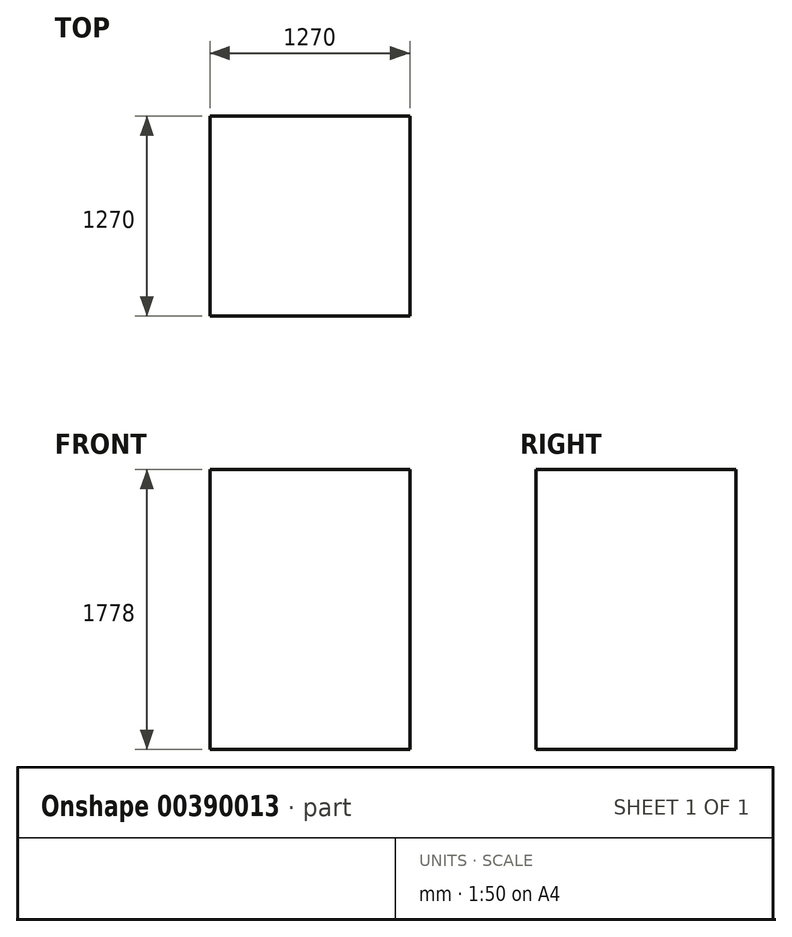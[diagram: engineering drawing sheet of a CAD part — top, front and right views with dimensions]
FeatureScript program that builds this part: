
annotation { "Feature Type Name" : "Feature", "Feature Type Description" : "" }
export const myFeature = defineFeature(function(context is Context, id is Id, definition is map)
    precondition{}
    {
        {
            var Q0;
            Q0=qCreatedBy(makeId("Top.planeOp"),FACE);
            var sketch = newSketch(context, id + "F0", { "sketchPlane" : qUnion([Q0])});
            skLineSegment(sketch, "E0.bottom", {"start": v(635, 635) * mm, "end": v(-635, 635) * mm});
            skLineSegment(sketch, "E0.top", {"start": v(635, -635) * mm, "end": v(-635, -635) * mm});
            skLineSegment(sketch, "E0.left", {"start": v(635, 635) * mm, "end": v(635, -635) * mm});
            skLineSegment(sketch, "E0.right", {"start": v(-635, 635) * mm, "end": v(-635, -635) * mm});
            skPoint(sketch, "E0.middle", {"position": v(0, 0) * mm});
            skSolve(sketch);
        }
        {
            var Q0;
            Q0 = qSketchRegion(id + "F0", true);
            extrude(context, id + "F1", {"entities" : qUnion([Q0]), "depth" : 1778 * mm});
        }
    });
